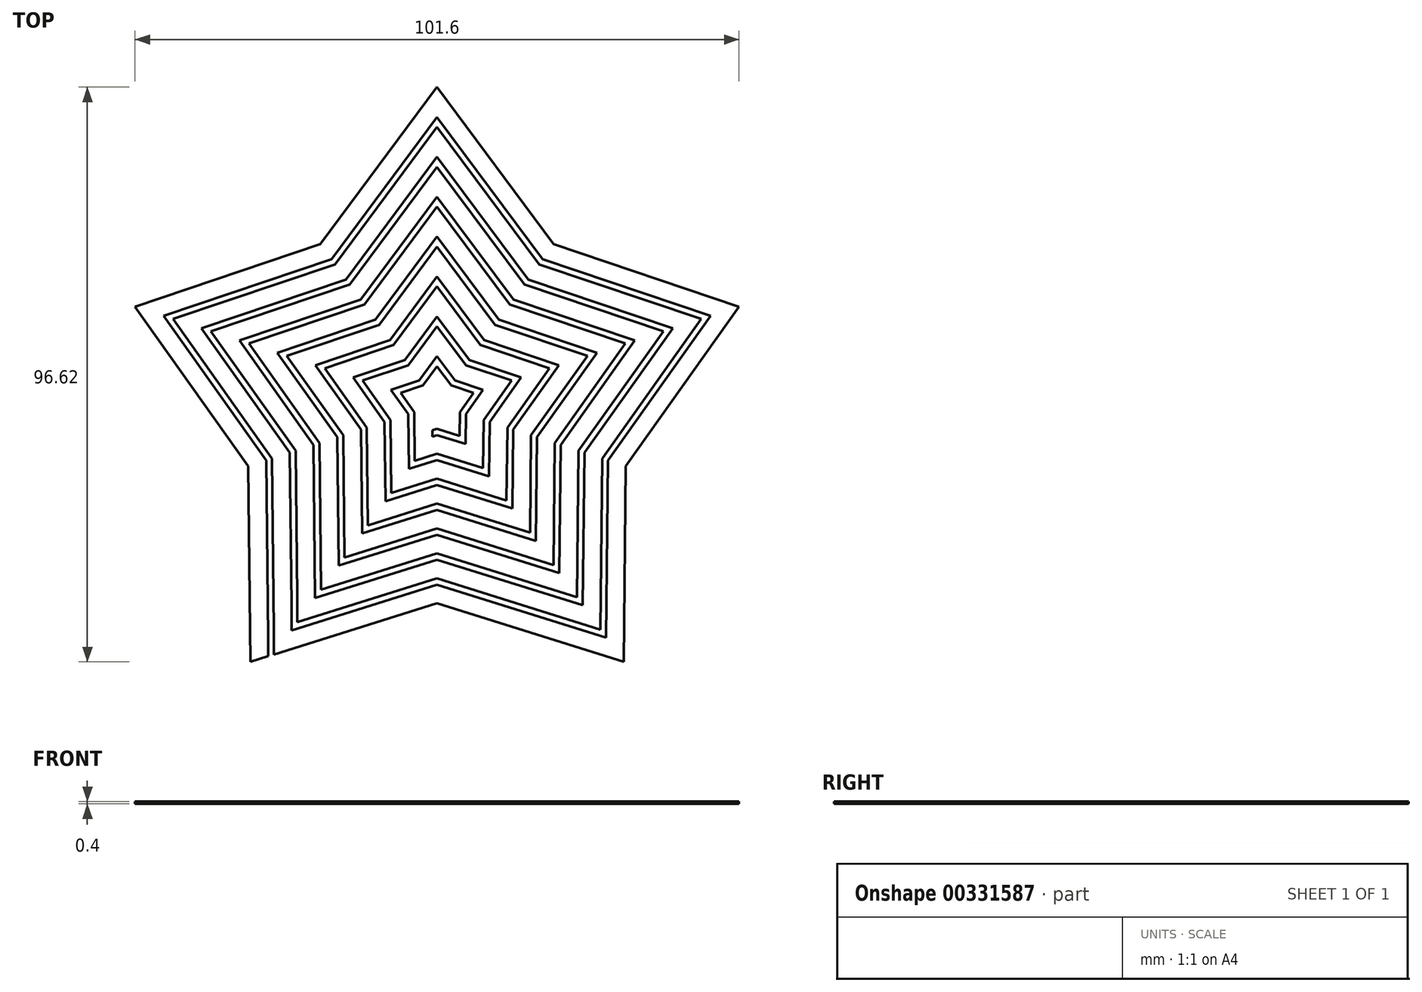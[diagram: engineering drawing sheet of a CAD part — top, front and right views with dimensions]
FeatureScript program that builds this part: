
annotation { "Feature Type Name" : "Feature", "Feature Type Description" : "" }
export const myFeature = defineFeature(function(context is Context, id is Id, definition is map)
    precondition{}
    {
        {
            var Q0;
            Q0=qCreatedBy(makeId("Top.planeOp"),FACE);
            var sketch = newSketch(context, id + "F0", { "sketchPlane" : qUnion([Q0])});
            skLineSegment(sketch, "E0", {"start": v(0, 40) * mm, "end": v(14.7, 20.23) * mm});
            skLineSegment(sketch, "E1", {"start": v(14.7, 20.23) * mm, "end": v(38.04, 12.36) * mm});
            skLineSegment(sketch, "E2", {"start": v(38.04, 12.36) * mm, "end": v(23.78, -7.73) * mm});
            skLineSegment(sketch, "E3", {"start": v(23.78, -7.73) * mm, "end": v(23.51, -32.36) * mm});
            skLineSegment(sketch, "E4", {"start": v(23.51, -32.36) * mm, "end": v(0, -25) * mm});
            skLineSegment(sketch, "E5", {"start": v(0, -25) * mm, "end": v(-19.52, -31.11) * mm});
            skLineSegment(sketch, "E6", {"start": v(-23.51, -32.36) * mm, "end": v(-23.78, -7.73) * mm});
            skLineSegment(sketch, "E7", {"start": v(-23.78, -7.73) * mm, "end": v(-38.04, 12.36) * mm});
            skLineSegment(sketch, "E8", {"start": v(-38.04, 12.36) * mm, "end": v(-14.7, 20.23) * mm});
            skLineSegment(sketch, "E9", {"start": v(-14.7, 20.23) * mm, "end": v(0, 40) * mm});
            skCircle(sketch, "E10", {"center": v(0, 0) * mm, "radius": 25 * mm, "construction": true});
            skLineSegment(sketch, "E11", {"start": v(0, 0) * mm, "end": v(38.04, 12.36) * mm, "construction": true});
            skLineSegment(sketch, "E12", {"start": v(0, 0) * mm, "end": v(23.51, -32.36) * mm, "construction": true});
            skLineSegment(sketch, "E13.0", {"start": v(-20.56, -28.3) * mm, "end": v(-20.79, -6.75) * mm});
            skLineSegment(sketch, "E13.1", {"start": v(0, -21.86) * mm, "end": v(-16.57, -27.04) * mm});
            skLineSegment(sketch, "E13.2", {"start": v(-20.79, -6.75) * mm, "end": v(-33.26, 10.8) * mm});
            skLineSegment(sketch, "E13.3", {"start": v(20.56, -28.3) * mm, "end": v(0, -21.86) * mm});
            skLineSegment(sketch, "E13.4", {"start": v(20.79, -6.75) * mm, "end": v(20.56, -28.3) * mm});
            skLineSegment(sketch, "E13.5", {"start": v(33.26, 10.8) * mm, "end": v(20.79, -6.75) * mm});
            skLineSegment(sketch, "E13.6", {"start": v(-33.26, 10.8) * mm, "end": v(-12.85, 17.68) * mm});
            skLineSegment(sketch, "E13.7", {"start": v(-12.85, 17.68) * mm, "end": v(0, 34.97) * mm});
            skLineSegment(sketch, "E13.8", {"start": v(0, 34.97) * mm, "end": v(12.85, 17.68) * mm});
            skLineSegment(sketch, "E13.9", {"start": v(12.85, 17.68) * mm, "end": v(33.26, 10.8) * mm});
            skLineSegment(sketch, "E14.0", {"start": v(0, -20.8) * mm, "end": v(-15.58, -25.69) * mm});
            skLineSegment(sketch, "E14.1", {"start": v(19.57, -26.94) * mm, "end": v(0, -20.8) * mm});
            skLineSegment(sketch, "E14.2", {"start": v(-19.57, -26.94) * mm, "end": v(-19.8, -6.43) * mm});
            skLineSegment(sketch, "E14.3", {"start": v(19.8, -6.43) * mm, "end": v(19.57, -26.94) * mm});
            skLineSegment(sketch, "E14.4", {"start": v(31.66, 10.29) * mm, "end": v(19.8, -6.43) * mm});
            skLineSegment(sketch, "E14.5", {"start": v(12.23, 16.83) * mm, "end": v(31.66, 10.29) * mm});
            skLineSegment(sketch, "E14.6", {"start": v(-19.8, -6.43) * mm, "end": v(-31.66, 10.29) * mm});
            skLineSegment(sketch, "E14.7", {"start": v(-31.66, 10.29) * mm, "end": v(-12.23, 16.83) * mm});
            skLineSegment(sketch, "E14.8", {"start": v(-12.23, 16.83) * mm, "end": v(0, 33.3) * mm});
            skLineSegment(sketch, "E14.9", {"start": v(0, 33.3) * mm, "end": v(12.23, 16.83) * mm});
            skLineSegment(sketch, "E15.0", {"start": v(-16.61, -22.87) * mm, "end": v(-16.8, -5.46) * mm});
            skLineSegment(sketch, "E15.1", {"start": v(0, -17.66) * mm, "end": v(-12.63, -21.62) * mm});
            skLineSegment(sketch, "E15.2", {"start": v(-16.8, -5.46) * mm, "end": v(-26.88, 8.73) * mm});
            skLineSegment(sketch, "E15.3", {"start": v(16.61, -22.87) * mm, "end": v(0, -17.66) * mm});
            skLineSegment(sketch, "E15.4", {"start": v(16.8, -5.46) * mm, "end": v(16.61, -22.87) * mm});
            skLineSegment(sketch, "E15.5", {"start": v(26.88, 8.73) * mm, "end": v(16.8, -5.46) * mm});
            skLineSegment(sketch, "E15.6", {"start": v(-26.88, 8.73) * mm, "end": v(-10.38, 14.3) * mm});
            skLineSegment(sketch, "E15.7", {"start": v(-10.38, 14.3) * mm, "end": v(0, 28.26) * mm});
            skLineSegment(sketch, "E15.8", {"start": v(0, 28.26) * mm, "end": v(10.38, 14.3) * mm});
            skLineSegment(sketch, "E15.9", {"start": v(10.38, 14.3) * mm, "end": v(26.88, 8.73) * mm});
            skLineSegment(sketch, "E16.0", {"start": v(-15.63, -21.5) * mm, "end": v(-15.8, -5.13) * mm});
            skLineSegment(sketch, "E16.1", {"start": v(0, -16.62) * mm, "end": v(-11.64, -20.26) * mm});
            skLineSegment(sketch, "E16.2", {"start": v(-15.8, -5.13) * mm, "end": v(-25.29, 8.22) * mm});
            skLineSegment(sketch, "E16.3", {"start": v(15.63, -21.5) * mm, "end": v(0, -16.62) * mm});
            skLineSegment(sketch, "E16.4", {"start": v(15.8, -5.13) * mm, "end": v(15.63, -21.5) * mm});
            skLineSegment(sketch, "E16.5", {"start": v(25.29, 8.22) * mm, "end": v(15.8, -5.13) * mm});
            skLineSegment(sketch, "E16.6", {"start": v(-25.29, 8.22) * mm, "end": v(-9.77, 13.44) * mm});
            skLineSegment(sketch, "E16.7", {"start": v(-9.77, 13.44) * mm, "end": v(0, 26.59) * mm});
            skLineSegment(sketch, "E16.8", {"start": v(0, 26.59) * mm, "end": v(9.77, 13.44) * mm});
            skLineSegment(sketch, "E16.9", {"start": v(9.77, 13.44) * mm, "end": v(25.29, 8.22) * mm});
            skLineSegment(sketch, "E17.0", {"start": v(-12.67, -17.44) * mm, "end": v(-12.81, -4.16) * mm});
            skLineSegment(sketch, "E17.1", {"start": v(0, -13.47) * mm, "end": v(-8.68, -16.2) * mm});
            skLineSegment(sketch, "E17.2", {"start": v(-12.81, -4.16) * mm, "end": v(-20.5, 6.66) * mm});
            skLineSegment(sketch, "E17.3", {"start": v(12.67, -17.44) * mm, "end": v(0, -13.47) * mm});
            skLineSegment(sketch, "E17.4", {"start": v(12.81, -4.16) * mm, "end": v(12.67, -17.44) * mm});
            skLineSegment(sketch, "E17.5", {"start": v(20.5, 6.66) * mm, "end": v(12.81, -4.16) * mm});
            skLineSegment(sketch, "E17.6", {"start": v(-20.5, 6.66) * mm, "end": v(-7.92, 10.9) * mm});
            skLineSegment(sketch, "E17.7", {"start": v(-7.92, 10.9) * mm, "end": v(0, 21.56) * mm});
            skLineSegment(sketch, "E17.8", {"start": v(0, 21.56) * mm, "end": v(7.92, 10.9) * mm});
            skLineSegment(sketch, "E17.9", {"start": v(7.92, 10.9) * mm, "end": v(20.5, 6.66) * mm});
            skLineSegment(sketch, "E18.0", {"start": v(-11.69, -16.08) * mm, "end": v(-11.82, -3.84) * mm});
            skLineSegment(sketch, "E18.1", {"start": v(0, -12.43) * mm, "end": v(-7.7, -14.84) * mm});
            skLineSegment(sketch, "E18.2", {"start": v(-11.82, -3.84) * mm, "end": v(-18.9, 6.14) * mm});
            skLineSegment(sketch, "E18.3", {"start": v(11.69, -16.08) * mm, "end": v(0, -12.43) * mm});
            skLineSegment(sketch, "E18.4", {"start": v(11.82, -3.84) * mm, "end": v(11.69, -16.08) * mm});
            skLineSegment(sketch, "E18.5", {"start": v(18.9, 6.14) * mm, "end": v(11.82, -3.84) * mm});
            skLineSegment(sketch, "E18.6", {"start": v(-18.9, 6.14) * mm, "end": v(-7.3, 10.05) * mm});
            skLineSegment(sketch, "E18.7", {"start": v(-7.3, 10.05) * mm, "end": v(0, 19.88) * mm});
            skLineSegment(sketch, "E18.8", {"start": v(0, 19.88) * mm, "end": v(7.3, 10.05) * mm});
            skLineSegment(sketch, "E18.9", {"start": v(7.3, 10.05) * mm, "end": v(18.9, 6.14) * mm});
            skLineSegment(sketch, "E19.0", {"start": v(-8.73, -12.01) * mm, "end": v(-8.83, -2.87) * mm});
            skLineSegment(sketch, "E19.1", {"start": v(0, -9.28) * mm, "end": v(-4.74, -10.77) * mm});
            skLineSegment(sketch, "E19.2", {"start": v(-8.83, -2.87) * mm, "end": v(-14.12, 4.59) * mm});
            skLineSegment(sketch, "E19.3", {"start": v(8.73, -12.01) * mm, "end": v(0, -9.28) * mm});
            skLineSegment(sketch, "E19.4", {"start": v(8.83, -2.87) * mm, "end": v(8.73, -12.01) * mm});
            skLineSegment(sketch, "E19.5", {"start": v(14.12, 4.59) * mm, "end": v(8.83, -2.87) * mm});
            skLineSegment(sketch, "E19.6", {"start": v(-14.12, 4.59) * mm, "end": v(-5.46, 7.5) * mm});
            skLineSegment(sketch, "E19.7", {"start": v(-5.46, 7.5) * mm, "end": v(0, 14.85) * mm});
            skLineSegment(sketch, "E19.8", {"start": v(0, 14.85) * mm, "end": v(5.46, 7.5) * mm});
            skLineSegment(sketch, "E19.9", {"start": v(5.46, 7.5) * mm, "end": v(14.12, 4.59) * mm});
            skLineSegment(sketch, "E20.0", {"start": v(-7.83, -2.54) * mm, "end": v(-12.53, 4.07) * mm});
            skLineSegment(sketch, "E20.1", {"start": v(-7.74, -10.66) * mm, "end": v(-7.83, -2.54) * mm});
            skLineSegment(sketch, "E20.2", {"start": v(-12.53, 4.07) * mm, "end": v(-4.84, 6.66) * mm});
            skLineSegment(sketch, "E20.3", {"start": v(0, -8.23) * mm, "end": v(-3.76, -9.41) * mm});
            skLineSegment(sketch, "E20.4", {"start": v(7.74, -10.66) * mm, "end": v(0, -8.23) * mm});
            skLineSegment(sketch, "E20.5", {"start": v(7.83, -2.54) * mm, "end": v(7.74, -10.66) * mm});
            skLineSegment(sketch, "E20.6", {"start": v(-4.84, 6.66) * mm, "end": v(0, 13.17) * mm});
            skLineSegment(sketch, "E20.7", {"start": v(0, 13.17) * mm, "end": v(4.84, 6.66) * mm});
            skLineSegment(sketch, "E20.8", {"start": v(4.84, 6.66) * mm, "end": v(12.53, 4.07) * mm});
            skLineSegment(sketch, "E20.9", {"start": v(12.53, 4.07) * mm, "end": v(7.83, -2.54) * mm});
            skLineSegment(sketch, "E21.0", {"start": v(-4.79, -6.59) * mm, "end": v(-4.84, -1.57) * mm});
            skLineSegment(sketch, "E21.1", {"start": v(0, -5.1) * mm, "end": v(-0.8, -5.34) * mm});
            skLineSegment(sketch, "E21.2", {"start": v(-4.84, -1.57) * mm, "end": v(-7.75, 2.52) * mm});
            skLineSegment(sketch, "E21.3", {"start": v(4.79, -6.59) * mm, "end": v(0, -5.1) * mm});
            skLineSegment(sketch, "E21.4", {"start": v(4.84, -1.57) * mm, "end": v(4.79, -6.59) * mm});
            skLineSegment(sketch, "E21.5", {"start": v(7.75, 2.52) * mm, "end": v(4.84, -1.57) * mm});
            skLineSegment(sketch, "E21.6", {"start": v(-7.75, 2.52) * mm, "end": v(-3, 4.12) * mm});
            skLineSegment(sketch, "E21.7", {"start": v(-3, 4.12) * mm, "end": v(0, 8.15) * mm});
            skLineSegment(sketch, "E21.8", {"start": v(0, 8.15) * mm, "end": v(3, 4.12) * mm});
            skLineSegment(sketch, "E21.9", {"start": v(3, 4.12) * mm, "end": v(7.75, 2.52) * mm});
            skLineSegment(sketch, "E22.0", {"start": v(0, -4.04) * mm, "end": v(-0.81, -4.3) * mm});
            skLineSegment(sketch, "E22.1", {"start": v(3.8, -5.23) * mm, "end": v(0, -4.04) * mm});
            skLineSegment(sketch, "E22.2", {"start": v(-3.8, -5.23) * mm, "end": v(-3.84, -1.25) * mm});
            skLineSegment(sketch, "E22.3", {"start": v(3.84, -1.25) * mm, "end": v(3.8, -5.23) * mm});
            skLineSegment(sketch, "E22.4", {"start": v(6.15, 2) * mm, "end": v(3.84, -1.25) * mm});
            skLineSegment(sketch, "E22.5", {"start": v(2.38, 3.27) * mm, "end": v(6.15, 2) * mm});
            skLineSegment(sketch, "E22.6", {"start": v(-3.84, -1.25) * mm, "end": v(-6.15, 2) * mm});
            skLineSegment(sketch, "E22.7", {"start": v(-6.15, 2) * mm, "end": v(-2.38, 3.27) * mm});
            skLineSegment(sketch, "E22.8", {"start": v(-2.38, 3.27) * mm, "end": v(0, 6.47) * mm});
            skLineSegment(sketch, "E22.9", {"start": v(0, 6.47) * mm, "end": v(2.38, 3.27) * mm});
            skLineSegment(sketch, "E23", {"start": v(-19.57, -26.94) * mm, "end": v(-19.52, -31.11) * mm});
            skLineSegment(sketch, "E24", {"start": v(-16.61, -22.87) * mm, "end": v(-16.57, -27.04) * mm});
            skLineSegment(sketch, "E25", {"start": v(-15.63, -21.5) * mm, "end": v(-15.58, -25.69) * mm});
            skLineSegment(sketch, "E26", {"start": v(-12.67, -17.44) * mm, "end": v(-12.63, -21.62) * mm});
            skLineSegment(sketch, "E27", {"start": v(-11.69, -16.08) * mm, "end": v(-11.64, -20.26) * mm});
            skLineSegment(sketch, "E28", {"start": v(-8.73, -12.01) * mm, "end": v(-8.68, -16.2) * mm});
            skLineSegment(sketch, "E29", {"start": v(-7.74, -10.66) * mm, "end": v(-7.7, -14.84) * mm});
            skLineSegment(sketch, "E30", {"start": v(-4.79, -6.59) * mm, "end": v(-4.74, -10.77) * mm});
            skLineSegment(sketch, "E31", {"start": v(-3.8, -5.23) * mm, "end": v(-3.76, -9.41) * mm});
            skLineSegment(sketch, "E32", {"start": v(-23.51, -32.36) * mm, "end": v(23.51, -32.36) * mm, "construction": true});
            skLineSegment(sketch, "E33", {"start": v(-0.81, -4.3) * mm, "end": v(-0.8, -5.34) * mm});
            skLineSegment(sketch, "E34.0", {"start": v(0, -26.05) * mm, "end": v(-20.51, -32.47) * mm});
            skLineSegment(sketch, "E34.1", {"start": v(-39.64, 12.88) * mm, "end": v(-15.31, 21.07) * mm});
            skLineSegment(sketch, "E34.2", {"start": v(-24.77, -8.05) * mm, "end": v(-39.64, 12.88) * mm});
            skLineSegment(sketch, "E34.3", {"start": v(-24.5, -33.72) * mm, "end": v(-24.77, -8.05) * mm});
            skLineSegment(sketch, "E34.5", {"start": v(-15.31, 21.07) * mm, "end": v(0, 41.68) * mm});
            skLineSegment(sketch, "E34.6", {"start": v(0, 41.68) * mm, "end": v(15.31, 21.07) * mm});
            skLineSegment(sketch, "E34.7", {"start": v(15.31, 21.07) * mm, "end": v(39.64, 12.88) * mm});
            skLineSegment(sketch, "E34.8", {"start": v(39.64, 12.88) * mm, "end": v(24.77, -8.05) * mm});
            skLineSegment(sketch, "E34.9", {"start": v(24.77, -8.05) * mm, "end": v(24.5, -33.72) * mm});
            skLineSegment(sketch, "E34.10", {"start": v(24.5, -33.72) * mm, "end": v(0, -26.05) * mm});
            skLineSegment(sketch, "E35.0", {"start": v(-27.76, -9.02) * mm, "end": v(-44.42, 14.43) * mm});
            skLineSegment(sketch, "E35.1", {"start": v(-27.45, -37.79) * mm, "end": v(-27.76, -9.02) * mm});
            skLineSegment(sketch, "E35.2", {"start": v(-44.42, 14.43) * mm, "end": v(-17.16, 23.62) * mm});
            skLineSegment(sketch, "E35.3", {"start": v(0, -29.2) * mm, "end": v(-23.51, -36.55) * mm});
            skLineSegment(sketch, "E35.4", {"start": v(27.45, -37.79) * mm, "end": v(0, -29.2) * mm});
            skLineSegment(sketch, "E35.5", {"start": v(27.76, -9.02) * mm, "end": v(27.45, -37.79) * mm});
            skLineSegment(sketch, "E35.6", {"start": v(-17.16, 23.62) * mm, "end": v(0, 46.7) * mm});
            skLineSegment(sketch, "E35.7", {"start": v(0, 46.7) * mm, "end": v(17.16, 23.62) * mm});
            skLineSegment(sketch, "E35.8", {"start": v(17.16, 23.62) * mm, "end": v(44.42, 14.43) * mm});
            skLineSegment(sketch, "E35.9", {"start": v(44.42, 14.43) * mm, "end": v(27.76, -9.02) * mm});
            skLineSegment(sketch, "E36.0", {"start": v(-28.76, -9.34) * mm, "end": v(-46.01, 14.95) * mm});
            skLineSegment(sketch, "E36.1", {"start": v(-28.44, -39.14) * mm, "end": v(-28.76, -9.34) * mm});
            skLineSegment(sketch, "E36.2", {"start": v(-46.01, 14.95) * mm, "end": v(-17.77, 24.46) * mm});
            skLineSegment(sketch, "E36.3", {"start": v(0, -30.24) * mm, "end": v(-24.5, -37.9) * mm});
            skLineSegment(sketch, "E36.4", {"start": v(28.44, -39.14) * mm, "end": v(0, -30.24) * mm});
            skLineSegment(sketch, "E36.5", {"start": v(28.76, -9.34) * mm, "end": v(28.44, -39.14) * mm});
            skLineSegment(sketch, "E36.6", {"start": v(-17.77, 24.46) * mm, "end": v(0, 48.38) * mm});
            skLineSegment(sketch, "E36.7", {"start": v(0, 48.38) * mm, "end": v(17.77, 24.46) * mm});
            skLineSegment(sketch, "E36.8", {"start": v(17.77, 24.46) * mm, "end": v(46.01, 14.95) * mm});
            skLineSegment(sketch, "E36.9", {"start": v(46.01, 14.95) * mm, "end": v(28.76, -9.34) * mm});
            skLineSegment(sketch, "E37.0", {"start": v(-31.75, -10.32) * mm, "end": v(-50.8, 16.5) * mm});
            skLineSegment(sketch, "E37.1", {"start": v(-31.4, -43.21) * mm, "end": v(-31.75, -10.32) * mm});
            skLineSegment(sketch, "E37.2", {"start": v(-50.8, 16.5) * mm, "end": v(-19.62, 27) * mm});
            skLineSegment(sketch, "E37.3", {"start": v(0, -33.38) * mm, "end": v(-27.45, -41.98) * mm});
            skLineSegment(sketch, "E37.4", {"start": v(31.4, -43.21) * mm, "end": v(0, -33.38) * mm});
            skLineSegment(sketch, "E37.5", {"start": v(31.75, -10.32) * mm, "end": v(31.4, -43.21) * mm});
            skLineSegment(sketch, "E37.6", {"start": v(-19.62, 27) * mm, "end": v(0, 53.41) * mm});
            skLineSegment(sketch, "E37.7", {"start": v(0, 53.41) * mm, "end": v(19.62, 27) * mm});
            skLineSegment(sketch, "E37.8", {"start": v(19.62, 27) * mm, "end": v(50.8, 16.5) * mm});
            skLineSegment(sketch, "E37.9", {"start": v(50.8, 16.5) * mm, "end": v(31.75, -10.32) * mm});
            skLineSegment(sketch, "E38", {"start": v(-28.44, -39.14) * mm, "end": v(-28.44, -42.29) * mm});
            skLineSegment(sketch, "E39", {"start": v(-27.45, -37.79) * mm, "end": v(-27.45, -41.98) * mm});
            skLineSegment(sketch, "E40.trimOffspring", {"start": v(-28.44, -42.29) * mm, "end": v(-31.4, -43.21) * mm});
            skLineSegment(sketch, "E41", {"start": v(-24.5, -33.72) * mm, "end": v(-24.5, -37.9) * mm});
            skLineSegment(sketch, "E42", {"start": v(-23.51, -32.36) * mm, "end": v(-23.51, -36.55) * mm});
            skLineSegment(sketch, "E43", {"start": v(-20.56, -28.3) * mm, "end": v(-20.51, -32.47) * mm});
            skSolve(sketch);
        }
        {
            var Q0;
            Q0=makeQuery(id+"F0.imprint","IMPRINT",FACE,{"disambiguationData":[TD([[makeQuery(id+"F0.imprint","IMPRINT",EDGE,{"derivedFrom":sQuery(id+"F0.wireOp",EDGE,"E0")}),-1.0]])]});
            extrude(context, id + "F1", {"entities" : qUnion([Q0]), "depth" : 0.4 * mm});
        }
    });
